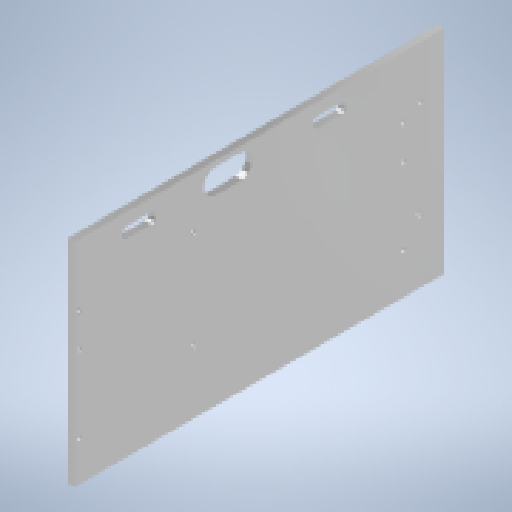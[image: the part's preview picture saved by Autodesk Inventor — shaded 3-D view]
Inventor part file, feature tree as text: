
AUTODESK INVENTOR PART (.ipt)
format: ipt  version: 2024.2 (Build 282272000, 272)  size: 188,928 bytes
history: native  units: mm
features: extrude x3, sketch x3, other x1
ambient origin geometry x8: Origin, YZ Plane, XZ Plane, XY Plane, X Axis, Y Axis, Z Axis, Center Point
bodies: Body1 (feature_tree)
feature tree (7):
  other  "Твердое тело1"
  extrude  "Выдавливание1"  Depth=204.0mm
  extrude  "Выдавливание2"  Depth=130.0mm
  extrude  "Выдавливание3"  Depth=3.0mm
  sketch  "Эскиз1"
  sketch  "Эскиз2"
  sketch  "Эскиз3"
